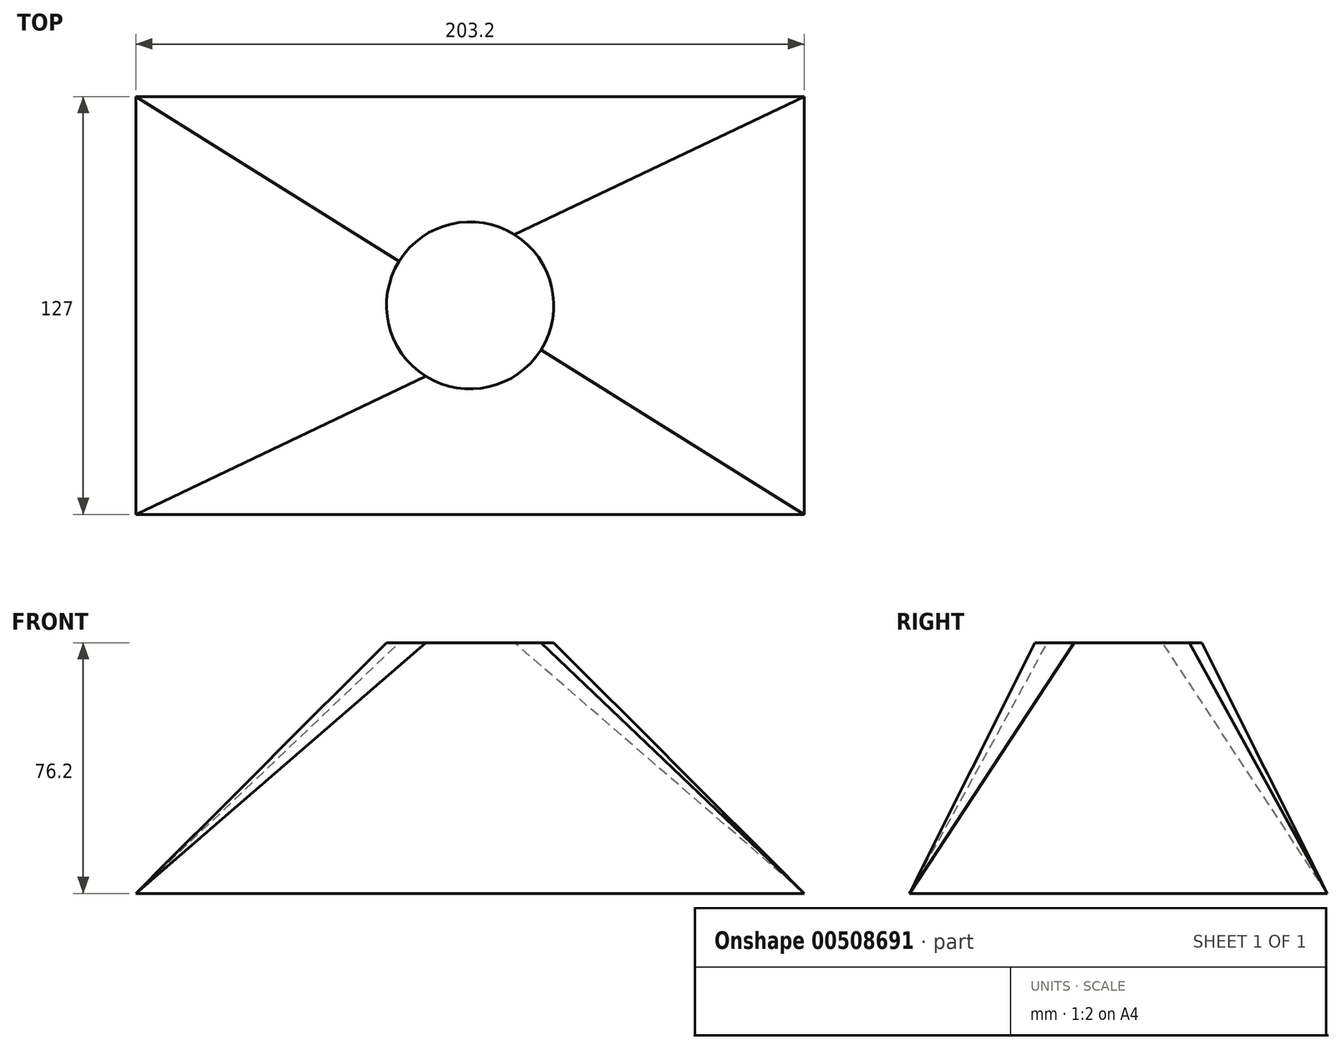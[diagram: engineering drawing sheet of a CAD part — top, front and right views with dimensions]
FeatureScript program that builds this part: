
annotation { "Feature Type Name" : "Feature", "Feature Type Description" : "" }
export const myFeature = defineFeature(function(context is Context, id is Id, definition is map)
    precondition{}
    {
        {
            var Q0;
            Q0=qCreatedBy(makeId("Top.planeOp"),FACE);
            var sketch = newSketch(context, id + "F0", { "sketchPlane" : qUnion([Q0])});
            skLineSegment(sketch, "E0.bottom", {"start": v(-101.6, 63.5) * mm, "end": v(101.6, 63.5) * mm});
            skLineSegment(sketch, "E0.top", {"start": v(-101.6, -63.5) * mm, "end": v(101.6, -63.5) * mm});
            skLineSegment(sketch, "E0.left", {"start": v(-101.6, 63.5) * mm, "end": v(-101.6, -63.5) * mm});
            skLineSegment(sketch, "E0.right", {"start": v(101.6, 63.5) * mm, "end": v(101.6, -63.5) * mm});
            skPoint(sketch, "E0.middle", {"position": v(0, 0) * mm});
            skSolve(sketch);
        }
        {
            var Q0;
            Q0=qCreatedBy(makeId("Top.planeOp"),FACE);
            cPlane(context, id + "F1", {"entities" : qUnion([Q0]), "cplaneType" : CPlaneType.OFFSET, "offset" : 76.2 * mm, "width" : 152.4 * mm, "height" : 152.4 * mm});
        }
        {
            var Q0;
            Q0=qCreatedBy(id+"F1.planeOp",FACE);
            var sketch = newSketch(context, id + "F2", { "sketchPlane" : qUnion([Q0])});
            skCircle(sketch, "E1", {"center": v(0, 0) * mm, "radius": 25.4 * mm});
            skSolve(sketch);
        }
        {
            var Q0;
            Q0=makeQuery(id+"F0.imprint","IMPRINT",FACE,{"disambiguationData":[TD([[makeQuery(id+"F0.imprint","IMPRINT",EDGE,{"derivedFrom":sQuery(id+"F0.wireOp",EDGE,"E0.bottom")}),-1.0]])]});
            var Q1;
            Q1=makeQuery(id+"F2.imprint","IMPRINT",FACE,{"disambiguationData":[TD([[makeQuery(id+"F2.imprint","IMPRINT",EDGE,{"derivedFrom":sQuery(id+"F2.wireOp",EDGE,"E1")}),1.0]])]});
            loft(context, id + "F3", {"sheetProfilesArray" : [{ "sheetProfileEntities" : qUnion([Q0]) }, { "sheetProfileEntities" : qUnion([Q1]) }]});
        }
    });
